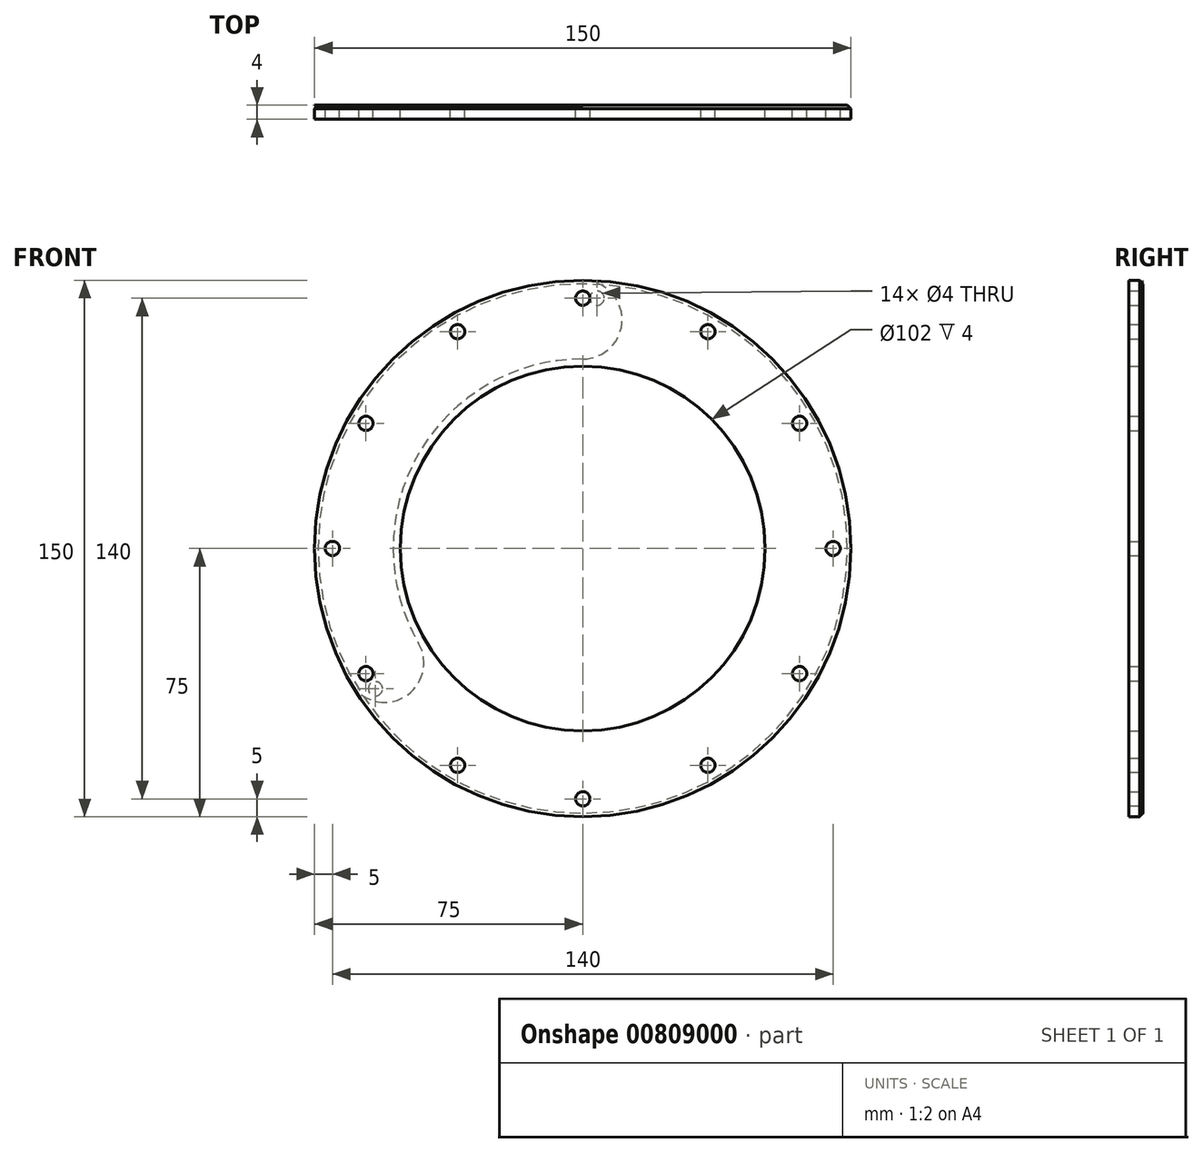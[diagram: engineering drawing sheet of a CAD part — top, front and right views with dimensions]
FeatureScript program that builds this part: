
annotation { "Feature Type Name" : "Feature", "Feature Type Description" : "" }
export const myFeature = defineFeature(function(context is Context, id is Id, definition is map)
    precondition{}
    {
        {
            var Q0;
            Q0=qCreatedBy(makeId("Front.planeOp"),FACE);
            var sketch = newSketch(context, id + "F0", { "sketchPlane" : qUnion([Q0])});
            skCircle(sketch, "E0", {"center": v(0, 0) * mm, "radius": 75 * mm});
            skCircle(sketch, "E1.0", {"center": v(0, 0) * mm, "radius": 51 * mm});
            skCircle(sketch, "E2", {"center": v(0, 70) * mm, "radius": 2 * mm});
            skCircle(sketch, "E3", {"center": v(0, 0) * mm, "radius": 7.5 * mm, "construction": true});
            skCircle(sketch, "E4.1.0", {"center": v(-35, 60.62) * mm, "radius": 2 * mm});
            skCircle(sketch, "E4.2.0", {"center": v(-60.62, 35) * mm, "radius": 2 * mm});
            skCircle(sketch, "E4.3.0", {"center": v(-70, 0) * mm, "radius": 2 * mm});
            skCircle(sketch, "E4.4.0", {"center": v(-60.62, -35) * mm, "radius": 2 * mm});
            skCircle(sketch, "E4.5.0", {"center": v(-35, -60.62) * mm, "radius": 2 * mm});
            skCircle(sketch, "E4.6.0", {"center": v(0, -70) * mm, "radius": 2 * mm});
            skCircle(sketch, "E4.7.0", {"center": v(35, -60.62) * mm, "radius": 2 * mm});
            skCircle(sketch, "E4.8.0", {"center": v(60.62, -35) * mm, "radius": 2 * mm});
            skCircle(sketch, "E4.9.0", {"center": v(70, 0) * mm, "radius": 2 * mm});
            skCircle(sketch, "E4.10.0", {"center": v(60.62, 35) * mm, "radius": 2 * mm});
            skCircle(sketch, "E4.11.0", {"center": v(35, 60.62) * mm, "radius": 2 * mm});
            skSolve(sketch);
        }
        {
            var Q0;
            Q0 = qSketchRegion(id + "F0", true);
            extrude(context, id + "F1", {"entities" : qUnion([Q0]), "depth" : 4 * mm, "offsetDistance" : 25 * mm});
        }
        {
            var Q0;
            Q0=makeQuery(id+"F1.opExtrude","CAP_EDGE",EDGE,{"disambiguationData":[OSD([sQuery(id+"F0.wireOp",EDGE,"E0")])],"isStart":true});
            chamfer(context, id + "F2", {"entities" : qUnion([Q0]), "width" : 1 * mm, "tangentPropagation" : true});
        }
        {
            var Q0;
            Q0=qCreatedBy(makeId("Front.planeOp"),FACE);
            var sketch = newSketch(context, id + "F3", { "sketchPlane" : qUnion([Q0])});
            skCircle(sketch, "E5", {"center": v(0, 0) * mm, "radius": 7.5 * mm, "construction": true});
            skLineSegment(sketch, "E6", {"start": v(0, 0) * mm, "end": v(0, 110) * mm, "construction": true});
            skLineSegment(sketch, "E7", {"start": v(0, 0) * mm, "end": v(-86.4, -49.89) * mm, "construction": true});
            skArc(sketch, "E8", {"start": v(0, 75) * mm, "mid": v(-64.95, 37.5) * mm, "end": v(-64.95, -37.5) * mm});
            skArc(sketch, "E9", {"start": v(0, 53) * mm, "mid": v(-45.9, 26.5) * mm, "end": v(-45.9, -26.5) * mm});
            skArc(sketch, "E10", {"start": v(0, 75) * mm, "mid": v(11, 64) * mm, "end": v(0, 53) * mm});
            skArc(sketch, "E11", {"start": v(-45.9, -26.5) * mm, "mid": v(-49.93, -41.53) * mm, "end": v(-64.95, -37.5) * mm});
            skCircle(sketch, "E12", {"center": v(4, 70) * mm, "radius": 2 * mm});
            skCircle(sketch, "E13", {"center": v(-57.97, -39.24) * mm, "radius": 2 * mm});
            skSolve(sketch);
        }
        {
            var Q0;
            Q0 = qSketchRegion(id + "F3", true);
            extrude(context, id + "F4", {"entities" : qUnion([Q0]), "depth" : .1 * mm, "offsetDistance" : 25 * mm});
        }
    });
